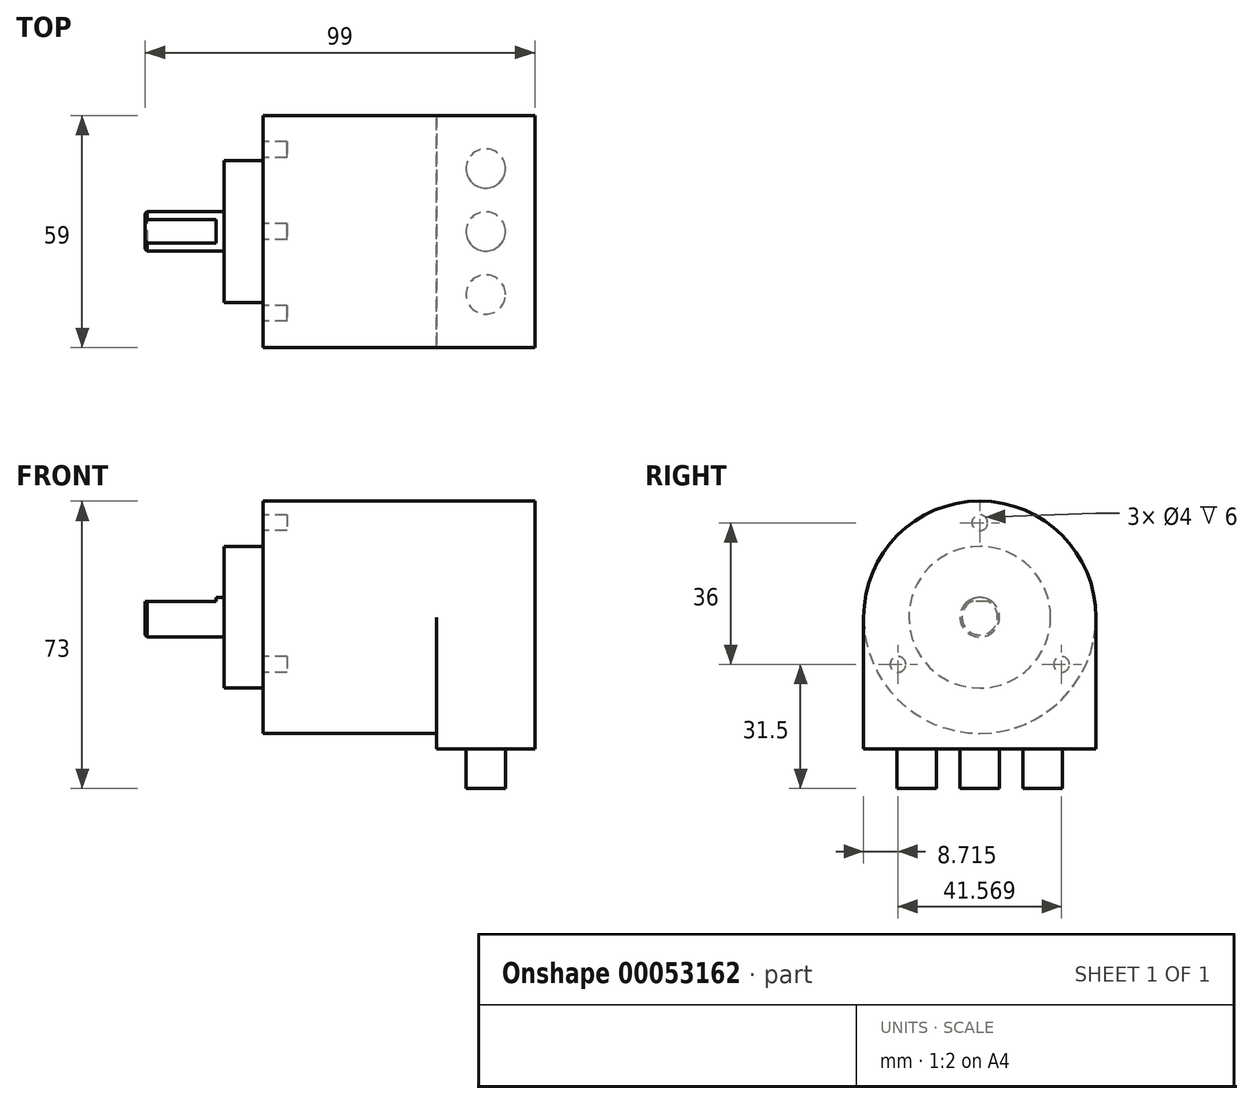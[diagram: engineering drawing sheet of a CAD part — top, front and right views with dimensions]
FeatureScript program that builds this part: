
annotation { "Feature Type Name" : "Feature", "Feature Type Description" : "" }
export const myFeature = defineFeature(function(context is Context, id is Id, definition is map)
    precondition{}
    {
        {
            var Q0;
            Q0=qCreatedBy(makeId("Right.planeOp"),FACE);
            var sketch = newSketch(context, id + "F0", { "sketchPlane" : qUnion([Q0])});
            skCircle(sketch, "E0", {"center": v(0, 0) * mm, "radius": 29.5 * mm});
            skSolve(sketch);
        }
        {
            var Q0;
            Q0 = qSketchRegion(id + "F0", true);
            extrude(context, id + "F1", {"entities" : qUnion([Q0]), "endBound" : BoundingType.SYMMETRIC, "depth" : 69 * mm});
        }
        {
            var Q0;
            Q0=makeQuery(id+"F1.opExtrude","CAP_FACE",FACE,{"disambiguationData":[OSD([sQuery(id+"F0.wireOp",EDGE,"E0")])],"isStart":true});
            var sketch = newSketch(context, id + "F2", { "sketchPlane" : qUnion([Q0])});
            skCircle(sketch, "E1", {"center": v(0, 0) * mm, "radius": 18 * mm});
            skSolve(sketch);
        }
        {
            var Q0;
            Q0 = qSketchRegion(id + "F2", true);
            extrude(context, id + "F3", {"entities" : qUnion([Q0]), "operationType" : NewBodyOperationType.ADD, "depth" : 10 * mm});
        }
        {
            var Q0;
            Q0=makeQuery(id+"F3.opExtrude","CAP_FACE",FACE,{"disambiguationData":[OSD([sQuery(id+"F2.wireOp",EDGE,"E1")])],"isStart":false});
            var sketch = newSketch(context, id + "F4", { "sketchPlane" : qUnion([Q0])});
            skCircle(sketch, "E2", {"center": v(0, 0) * mm, "radius": 5 * mm});
            skSolve(sketch);
        }
        {
            var Q0;
            Q0 = qSketchRegion(id + "F4", true);
            extrude(context, id + "F5", {"entities" : qUnion([Q0]), "operationType" : NewBodyOperationType.ADD, "depth" : 20 * mm});
        }
        {
            var Q0;
            Q0=makeQuery(id+"F1.opExtrude","CAP_FACE",FACE,{"disambiguationData":[OSD([sQuery(id+"F0.wireOp",EDGE,"E0")])],"isStart":false});
            var sketch = newSketch(context, id + "F6", { "sketchPlane" : qUnion([Q0])});
            skArc(sketch, "E3.0", {"start": v(29.5, 0) * mm, "mid": v(0, 29.5) * mm, "end": v(-29.5, 0) * mm});
            skLineSegment(sketch, "E4", {"start": v(0, 29.5) * mm, "end": v(-63.49, 29.5) * mm, "construction": true});
            skLineSegment(sketch, "E5.0", {"start": v(0, -58.5) * mm, "end": v(-63.49, -58.5) * mm, "construction": true});
            skLineSegment(sketch, "E6.0", {"start": v(29.5, -33.5) * mm, "end": v(-29.5, -33.5) * mm});
            skLineSegment(sketch, "E7", {"start": v(-29.5, 0) * mm, "end": v(-29.5, -33.5) * mm});
            skLineSegment(sketch, "E8", {"start": v(0, 0) * mm, "end": v(0, 88.53) * mm, "construction": true});
            skLineSegment(sketch, "E9.MirrorCS", {"start": v(29.5, 0) * mm, "end": v(29.5, -33.5) * mm});
            skSolve(sketch);
        }
        {
            var Q0;
            Q0 = qSketchRegion(id + "F6", true);
            extrude(context, id + "F7", {"entities" : qUnion([Q0]), "operationType" : NewBodyOperationType.ADD, "oppositeDirection" : true, "depth" : 25 * mm});
        }
        {
            var Q0;
            Q0=makeQuery(id+"F7.opExtrude","SWEPT_FACE",FACE,{"disambiguationData":[OSD([sQuery(id+"F6.wireOp",EDGE,"E6.0")])]});
            var sketch = newSketch(context, id + "F8", { "sketchPlane" : qUnion([Q0])});
            skLineSegment(sketch, "E10", {"start": v(22, 29.5) * mm, "end": v(22, -29.5) * mm, "construction": true});
            skLineSegment(sketch, "E11", {"start": v(34.5, 0) * mm, "end": v(9.5, 0) * mm, "construction": true});
            skLineSegment(sketch, "E12.0", {"start": v(34.5, 16) * mm, "end": v(9.5, 16) * mm, "construction": true});
            skCircle(sketch, "E13", {"center": v(22, 16) * mm, "radius": 5 * mm});
            skCircle(sketch, "E14", {"center": v(22, 0) * mm, "radius": 5 * mm});
            skCircle(sketch, "E15.MirrorC", {"center": v(22, -16) * mm, "radius": 5 * mm});
            skSolve(sketch);
        }
        {
            var Q0;
            Q0 = qSketchRegion(id + "F8", true);
            extrude(context, id + "F9", {"entities" : qUnion([Q0]), "operationType" : NewBodyOperationType.ADD, "depth" : 10 * mm});
        }
        {
            var Q0;
            Q0=makeQuery(id+"F1.opExtrude","CAP_FACE",FACE,{"disambiguationData":[OSD([sQuery(id+"F0.wireOp",EDGE,"E0")])],"isStart":true});
            var sketch = newSketch(context, id + "F10", { "sketchPlane" : qUnion([Q0])});
            skCircle(sketch, "E16", {"center": v(0, 0) * mm, "radius": 24 * mm, "construction": true});
            skLineSegment(sketch, "E17", {"start": v(0, 0) * mm, "end": v(0, 35.88) * mm, "construction": true});
            skCircle(sketch, "E18", {"center": v(0, 24) * mm, "radius": 2 * mm});
            skCircle(sketch, "E19.1.0", {"center": v(-20.78, -12) * mm, "radius": 2 * mm});
            skCircle(sketch, "E19.2.0", {"center": v(20.78, -12) * mm, "radius": 2 * mm});
            skSolve(sketch);
        }
        {
            var Q0;
            Q0=makeQuery(id+"F10.imprint","IMPRINT",FACE,{"disambiguationData":[TD([[makeQuery(id+"F10.imprint","IMPRINT",EDGE,{"derivedFrom":sQuery(id+"F10.wireOp",EDGE,"E19.1.0")}),1.0]])]});
            var Q1;
            Q1=makeQuery(id+"F10.imprint","IMPRINT",FACE,{"disambiguationData":[TD([[makeQuery(id+"F10.imprint","IMPRINT",EDGE,{"derivedFrom":sQuery(id+"F10.wireOp",EDGE,"E18")}),1.0]])]});
            var Q2;
            Q2=makeQuery(id+"F10.imprint","IMPRINT",FACE,{"disambiguationData":[TD([[makeQuery(id+"F10.imprint","IMPRINT",EDGE,{"derivedFrom":sQuery(id+"F10.wireOp",EDGE,"E19.2.0")}),1.0]])]});
            extrude(context, id + "F11", {"entities" : qUnion([Q0, Q1, Q2]), "operationType" : NewBodyOperationType.REMOVE, "oppositeDirection" : true, "depth" : 6 * mm});
        }
        {
            var Q0;
            Q0=qCreatedBy(makeId("Front.planeOp"),FACE);
            var sketch = newSketch(context, id + "F12", { "sketchPlane" : qUnion([Q0])});
            skLineSegment(sketch, "E20", {"start": v(-44.5, -5) * mm, "end": v(-64.5, -5) * mm, "construction": true});
            skLineSegment(sketch, "E21", {"start": v(-64.5, 5) * mm, "end": v(-44.5, 5) * mm});
            skLineSegment(sketch, "E22.0", {"start": v(-64.5, 4) * mm, "end": v(-44.5, 4) * mm});
            skLineSegment(sketch, "E23.bottom", {"start": v(-64.5, 5) * mm, "end": v(-46.5, 5) * mm});
            skLineSegment(sketch, "E23.top", {"start": v(-64.5, 4) * mm, "end": v(-46.5, 4) * mm});
            skLineSegment(sketch, "E23.left", {"start": v(-64.5, 5) * mm, "end": v(-64.5, 4) * mm});
            skLineSegment(sketch, "E23.right", {"start": v(-46.5, 5) * mm, "end": v(-46.5, 4) * mm});
            skSolve(sketch);
        }
        {
            var Q0;
            Q0 = qSketchRegion(id + "F12", true);
            extrude(context, id + "F13", {"entities" : qUnion([Q0]), "operationType" : NewBodyOperationType.REMOVE, "endBound" : BoundingType.SYMMETRIC, "oppositeDirection" : true, "depth" : 25 * mm});
        }
        {
            var Q0;
            Q0=makeQuery(id+"F5.opExtrude","CAP_EDGE",EDGE,{"disambiguationData":[OSD([sQuery(id+"F4.wireOp",EDGE,"E2")])],"isStart":false});
            chamfer(context, id + "F14", {"entities" : qUnion([Q0]), "width" : .5 * mm, "tangentPropagation" : true});
        }
    });
